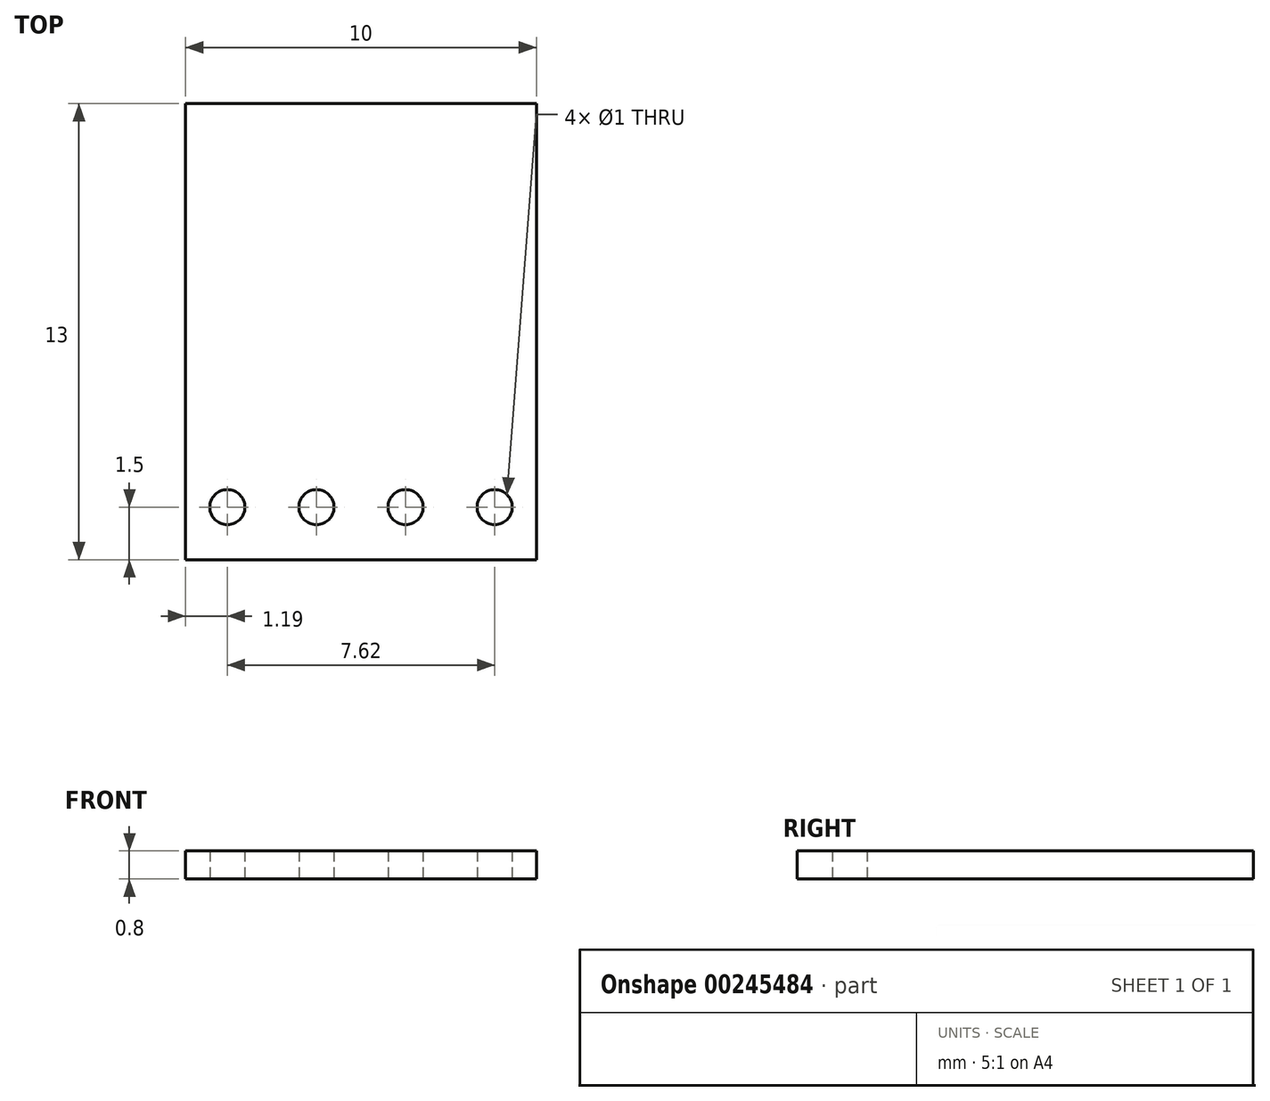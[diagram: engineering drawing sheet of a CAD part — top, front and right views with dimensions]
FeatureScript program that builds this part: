
annotation { "Feature Type Name" : "Feature", "Feature Type Description" : "" }
export const myFeature = defineFeature(function(context is Context, id is Id, definition is map)
    precondition{}
    {
        {
            var Q0;
            Q0=qCreatedBy(makeId("Top.planeOp"),FACE);
            var sketch = newSketch(context, id + "F0", { "sketchPlane" : qUnion([Q0])});
            skLineSegment(sketch, "E0.bottom", {"start": v(5, -6.5) * mm, "end": v(-5, -6.5) * mm});
            skLineSegment(sketch, "E0.top", {"start": v(5, 6.5) * mm, "end": v(-5, 6.5) * mm});
            skLineSegment(sketch, "E0.left", {"start": v(5, -6.5) * mm, "end": v(5, 6.5) * mm});
            skLineSegment(sketch, "E0.right", {"start": v(-5, -6.5) * mm, "end": v(-5, 6.5) * mm});
            skPoint(sketch, "E0.middle", {"position": v(0, 0) * mm});
            skCircle(sketch, "E1", {"center": v(-3.8, -5) * mm, "radius": 0.5 * mm});
            skCircle(sketch, "E2.1.0.0", {"center": v(-1.27, -5) * mm, "radius": 0.5 * mm});
            skCircle(sketch, "E2.2.0.0", {"center": v(1.27, -5) * mm, "radius": 0.5 * mm});
            skCircle(sketch, "E2.3.0.0", {"center": v(3.81, -5) * mm, "radius": 0.5 * mm});
            skLineSegment(sketch, "E2.direction1", {"start": v(-3.8, -5) * mm, "end": v(-1.27, -5) * mm, "construction": true});
            skSolve(sketch);
        }
        {
            var Q0;
            Q0=makeQuery(id+"F0.imprint","IMPRINT",FACE,{"disambiguationData":[TD([[makeQuery(id+"F0.imprint","IMPRINT",EDGE,{"derivedFrom":sQuery(id+"F0.wireOp",EDGE,"E0.bottom")}),-1.0]])]});
            extrude(context, id + "F1", {"entities" : qUnion([Q0]), "depth" : 0.8 * mm});
        }
    });
